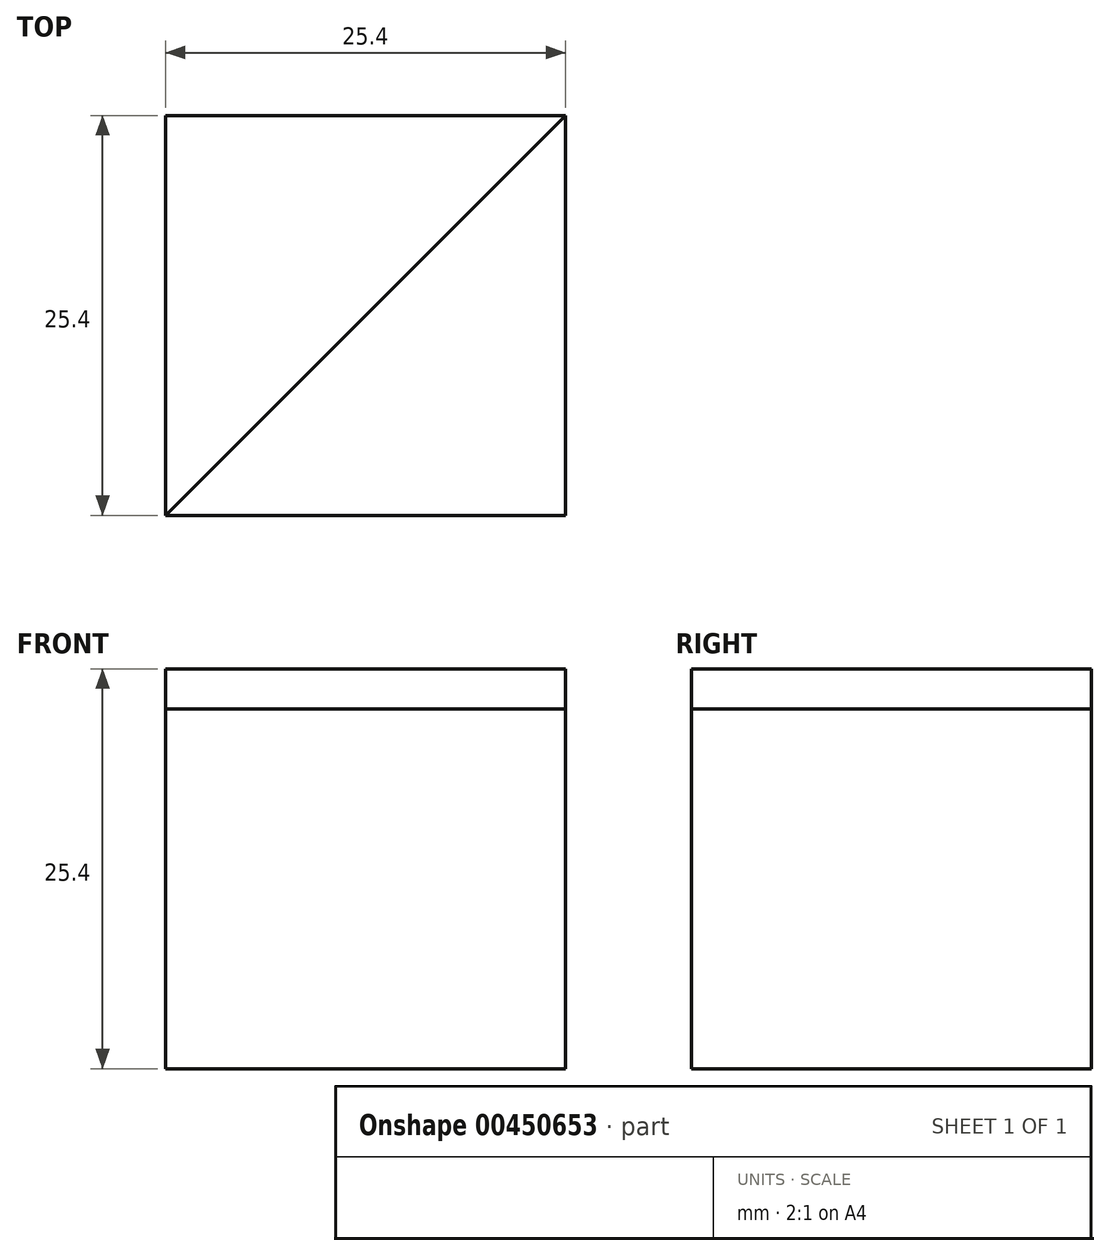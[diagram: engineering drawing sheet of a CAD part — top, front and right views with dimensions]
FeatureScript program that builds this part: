
annotation { "Feature Type Name" : "Feature", "Feature Type Description" : "" }
export const myFeature = defineFeature(function(context is Context, id is Id, definition is map)
    precondition{}
    {
        {
            var Q0;
            Q0=qCreatedBy(makeId("Top.planeOp"),FACE);
            var sketch = newSketch(context, id + "F0", { "sketchPlane" : qUnion([Q0])});
            skLineSegment(sketch, "E0.bottom", {"start": v(0, -1.47) * mm, "end": v(25.4, -1.47) * mm});
            skLineSegment(sketch, "E0.top", {"start": v(0, -26.87) * mm, "end": v(25.4, -26.87) * mm});
            skLineSegment(sketch, "E0.left", {"start": v(0, -1.47) * mm, "end": v(0, -26.87) * mm});
            skLineSegment(sketch, "E0.right", {"start": v(25.4, -1.47) * mm, "end": v(25.4, -26.87) * mm});
            skSolve(sketch);
        }
        {
            var Q0;
            Q0 = qSketchRegion(id + "F0", true);
            extrude(context, id + "F1", {"entities" : qUnion([Q0]), "depth" : 25.4 * mm});
        }
        {
            var Q0;
            Q0=makeQuery(id+"F1.opExtrude","CAP_FACE",FACE,{"disambiguationData":[OSD([sQuery(id+"F0.wireOp",EDGE,"E0.bottom"),sQuery(id+"F0.wireOp",EDGE,"E0.top"),sQuery(id+"F0.wireOp",EDGE,"E0.left"),sQuery(id+"F0.wireOp",EDGE,"E0.right")])],"isStart":false});
            var sketch = newSketch(context, id + "F2", { "sketchPlane" : qUnion([Q0])});
            skLineSegment(sketch, "E1", {"start": v(0, -1.47) * mm, "end": v(25.4, -26.87) * mm});
            skLineSegment(sketch, "E2", {"start": v(0, -26.87) * mm, "end": v(25.4, -1.47) * mm});
            skCircle(sketch, "E3", {"center": v(12.7, -14.17) * mm, "radius": 2.54 * mm});
            skSolve(sketch);
        }
        {
            var Q0;
            {var subQ0=sQuery(id+"F2.wireOp",EDGE,"E2");var subQ1=sQuery(id+"F2.wireOp",EDGE,"E1");var subQ2=makeQuery(id+"F2.imprint","INTERSECT",VERTEX,{"derivedFrom":[subQ1,subQ0]});Q0=makeQuery(id+"F2.imprint","IMPRINT",FACE,{"disambiguationData":[TD([[makeQuery(id+"F2.imprint","IMPRINT",EDGE,{"disambiguationData":[TD([[subQ2,-1.0]])],"derivedFrom":subQ1}),-1.0]])]});}
            var Q1;
            {var subQ0=sQuery(id+"F2.wireOp",EDGE,"E2");var subQ1=sQuery(id+"F2.wireOp",EDGE,"E1");var subQ2=makeQuery(id+"F2.imprint","INTERSECT",VERTEX,{"derivedFrom":[subQ1,subQ0]});Q1=makeQuery(id+"F2.imprint","IMPRINT",FACE,{"disambiguationData":[TD([[makeQuery(id+"F2.imprint","IMPRINT",EDGE,{"disambiguationData":[TD([[subQ2,-1.0]])],"derivedFrom":subQ1}),1.0]])]});}
            var Q2;
            {var subQ0=sQuery(id+"F2.wireOp",EDGE,"E3");var subQ1=sQuery(id+"F2.wireOp",EDGE,"E1");var subQ2=makeQuery(id+"F2.imprint","INTERSECT",VERTEX,{"disambiguationData":[OD(0.0)],"derivedFrom":[subQ1,subQ0]});Q2=makeQuery(id+"F2.imprint","IMPRINT",FACE,{"disambiguationData":[TD([[makeQuery(id+"F2.imprint","IMPRINT",EDGE,{"disambiguationData":[TD([[subQ2,-1.0]])],"derivedFrom":subQ1}),1.0]])]});}
            var Q3;
            {var subQ0=sQuery(id+"F2.wireOp",EDGE,"E3");var subQ1=sQuery(id+"F2.wireOp",EDGE,"E1");var subQ2=makeQuery(id+"F2.imprint","INTERSECT",VERTEX,{"disambiguationData":[OD(0.0)],"derivedFrom":[subQ1,subQ0]});Q3=makeQuery(id+"F2.imprint","IMPRINT",FACE,{"disambiguationData":[TD([[makeQuery(id+"F2.imprint","IMPRINT",EDGE,{"disambiguationData":[TD([[subQ2,-1.0]])],"derivedFrom":subQ1}),-1.0]])]});}
            extrude(context, id + "F3", {"entities" : qUnion([Q0, Q1, Q2, Q3]), "operationType" : NewBodyOperationType.REMOVE, "oppositeDirection" : true, "depth" : 2.54 * mm});
        }
    });
